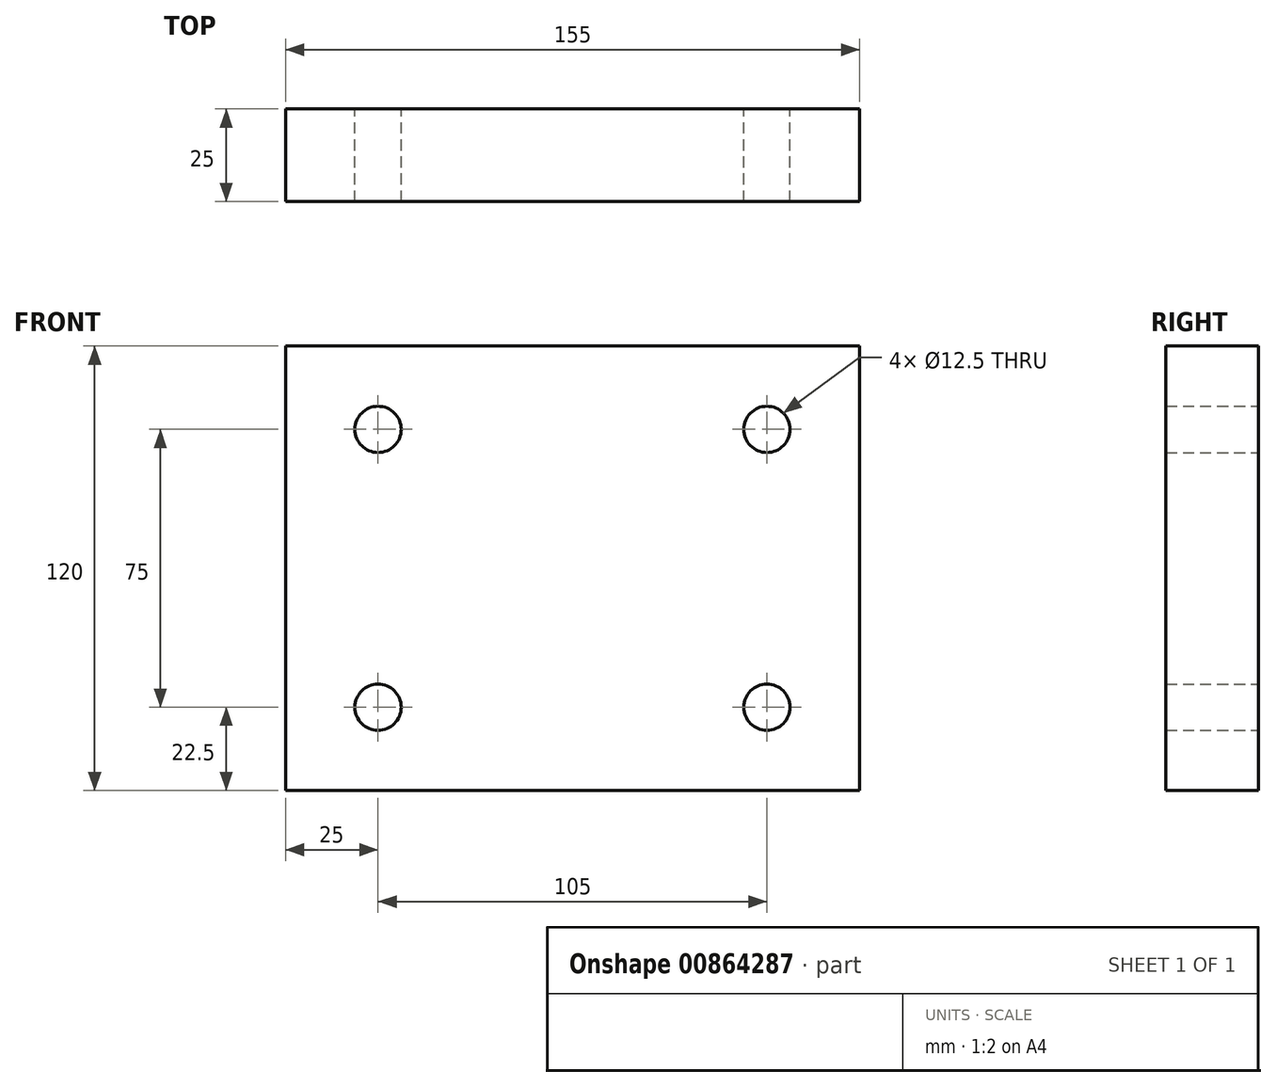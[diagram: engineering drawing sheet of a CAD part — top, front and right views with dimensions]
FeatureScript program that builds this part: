
annotation { "Feature Type Name" : "Feature", "Feature Type Description" : "" }
export const myFeature = defineFeature(function(context is Context, id is Id, definition is map)
    precondition{}
    {
        {
            var Q0;
            Q0=qCreatedBy(makeId("Front.planeOp"),FACE);
            var sketch = newSketch(context, id + "F0", { "sketchPlane" : qUnion([Q0])});
            skLineSegment(sketch, "E0.bottom", {"start": v(-77.5, 60) * mm, "end": v(77.5, 60) * mm});
            skLineSegment(sketch, "E0.top", {"start": v(-77.5, -60) * mm, "end": v(77.5, -60) * mm});
            skLineSegment(sketch, "E0.left", {"start": v(-77.5, 60) * mm, "end": v(-77.5, -60) * mm});
            skLineSegment(sketch, "E0.right", {"start": v(77.5, 60) * mm, "end": v(77.5, -60) * mm});
            skPoint(sketch, "E0.middle", {"position": v(0, 0) * mm});
            skLineSegment(sketch, "E1", {"start": v(0, 128.88) * mm, "end": v(0, -117.24) * mm, "construction": true});
            skPoint(sketch, "E1.startSnap0", {"position": v(0, 60) * mm});
            skLineSegment(sketch, "E2", {"start": v(-143.37, 0) * mm, "end": v(173.88, 0) * mm, "construction": true});
            skPoint(sketch, "E2.startSnap0", {"position": v(-77.5, 0) * mm});
            skLineSegment(sketch, "E3", {"start": v(-132.7, -37.5) * mm, "end": v(149.7, -37.5) * mm, "construction": true});
            skLineSegment(sketch, "E4", {"start": v(-116.34, 37.5) * mm, "end": v(163.92, 37.5) * mm, "construction": true});
            skLineSegment(sketch, "E5", {"start": v(-52.5, 89.75) * mm, "end": v(-52.5, -104.43) * mm, "construction": true});
            skLineSegment(sketch, "E6", {"start": v(52.5, 87.62) * mm, "end": v(52.5, -104.43) * mm, "construction": true});
            skCircle(sketch, "E7", {"center": v(52.5, -37.5) * mm, "radius": 6.25 * mm});
            skCircle(sketch, "E8", {"center": v(-52.5, -37.5) * mm, "radius": 6.25 * mm});
            skCircle(sketch, "E9", {"center": v(-52.5, 37.5) * mm, "radius": 6.25 * mm});
            skCircle(sketch, "E10", {"center": v(52.5, 37.5) * mm, "radius": 6.25 * mm});
            skSolve(sketch);
        }
        {
            var Q0;
            Q0=makeQuery(id+"F0.imprint","IMPRINT",FACE,{"disambiguationData":[TD([[makeQuery(id+"F0.imprint","IMPRINT",EDGE,{"derivedFrom":sQuery(id+"F0.wireOp",EDGE,"E0.bottom")}),-1.0]])]});
            extrude(context, id + "F1", {"entities" : qUnion([Q0]), "depth" : 25 * mm, "offsetDistance" : 25 * mm});
        }
    });
